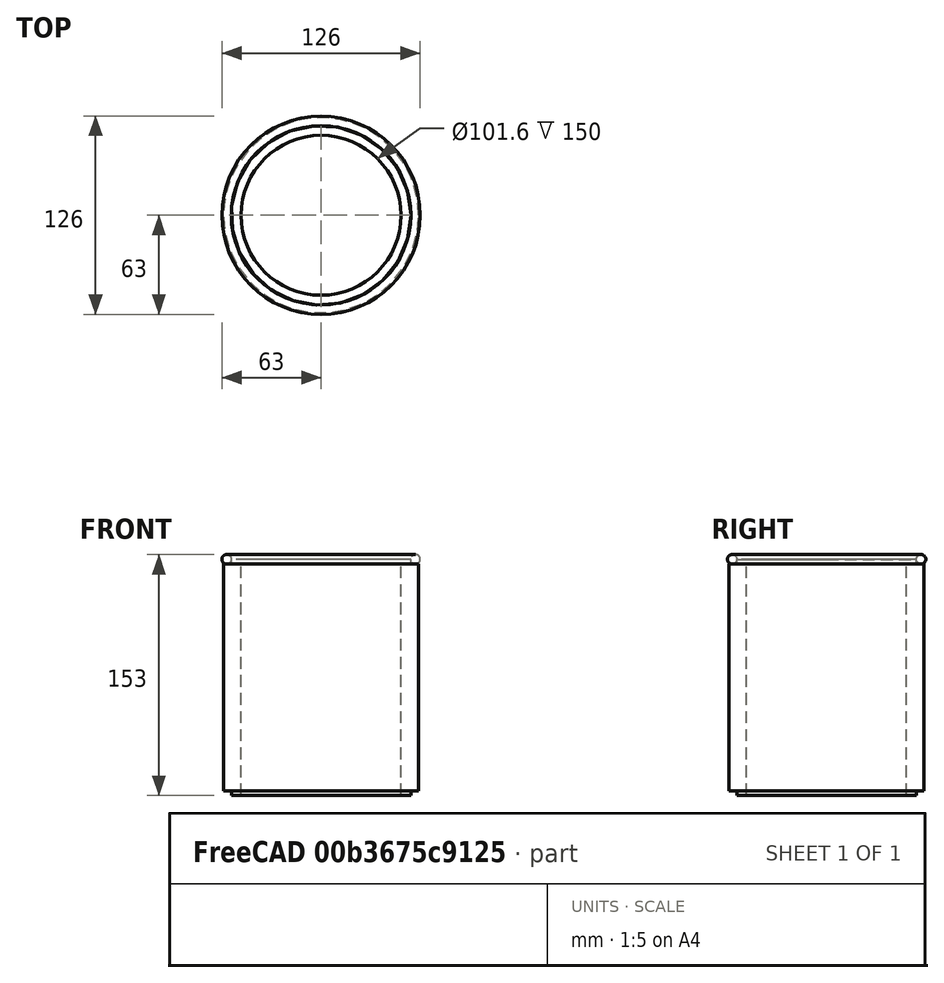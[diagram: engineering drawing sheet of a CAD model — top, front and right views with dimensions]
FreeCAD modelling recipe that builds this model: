
FCSTD DOCUMENT  (FreeCAD 0.17R13519 (Git))
Label: tube cad design
License: All rights reserved
LicenseURL: http://en.wikipedia.org/wiki/All_rights_reserved
objects: Part::Cylinder×18, Part::Cut×15, TechDraw::DrawViewDimension×7, TechDraw::DrawViewPart×5, Part::Torus×1, TechDraw::DrawSVGTemplate×1, TechDraw::DrawPage×1
note: 34 computed .brp shape members not serialized (recipe doc carries the construction recipe); baked Part::Feature solids carry a one-line shape summary decoded from their .brp

FEATURE [Part::Cylinder] Cylinder
  Angle = 360
  AttacherType = Attacher::AttachEngine3D
  Height = 150
  Radius = 61.91
FEATURE [Part::Cylinder] Cylinder001
  Angle = 360
  AttacherType = Attacher::AttachEngine3D
  Height = 150
  Radius = 50.8
FEATURE [Part::Cut] Cut
  Base = -> Cylinder
  Tool = -> Cylinder001
FEATURE [Part::Cylinder] Cylinder002
  Angle = 360
  AttacherType = Attacher::AttachEngine3D
  Height = 3
  Radius = 61.91
FEATURE [Part::Cylinder] Cylinder003
  Angle = 360
  AttacherType = Attacher::AttachEngine3D
  Height = 3
  Radius = 57
FEATURE [Part::Cut] Cut001
  Base = -> Cylinder002
  Tool = -> Cylinder003
FEATURE [Part::Cylinder] Cylinder004
  Angle = 360
  AttacherType = Attacher::AttachEngine3D
  Height = 3
  Radius = 61.91
FEATURE [Part::Cylinder] Cylinder005
  Angle = 360
  AttacherType = Attacher::AttachEngine3D
  Height = 3
  Radius = 57
FEATURE [Part::Cut] Cut002
  Base = -> Cylinder004
  Placement = pos=(0,0,147) rot=(0,0,1;0rad)
  Tool = -> Cylinder005
FEATURE [Part::Cut] Cut003
  Base = -> Cut
  Tool = -> Cut002
FEATURE [Part::Cut] Cut004
  Base = -> Cut003
  Placement = pos=(100,-500,0) rot=(0.707107,0,0.707107;0rad)
  Tool = -> Cut001
FEATURE [Part::Torus] Torus
  Angle1 = -180
  Angle2 = 180
  Angle3 = 360
  AttacherType = Attacher::AttachEngine3D
  Placement = pos=(100,-500,150) rot=(0,0,1;0rad)
  Radius1 = 60
  Radius2 = 3
FEATURE [TechDraw::DrawSVGTemplate] Template001
  EditableTexts = Designed_by_Name=Jake Hosen; FC-Date=July 2018; FC-Title=Title; Subtitle=Case Tube
  Height = 210
  Orientation = 1
  Width = 297
FEATURE [TechDraw::DrawViewPart] View003
  CoarseView = false
  Direction = (0,0,1)
  Focus = 100
  HardHidden = false
  IsoCount = 0
  IsoHidden = false
  IsoVisible = false
  LockPosition = false
  Perspective = false
  Rotation = 0
  Scale = 0.5
  ScaleType = 0
  SeamHidden = false
  SeamVisible = false
  SmoothHidden = false
  SmoothVisible = false
  Source = -> [Cut004]
  X = 78.5627
  Y = 140.236
FEATURE [TechDraw::DrawViewPart] View004
  CoarseView = false
  Direction = (-1,1,0)
  Focus = 100
  HardHidden = false
  IsoCount = 0
  IsoHidden = false
  IsoVisible = false
  LockPosition = false
  Perspective = false
  Rotation = 90
  Scale = 0.5
  ScaleType = 0
  SeamHidden = false
  SeamVisible = false
  SmoothHidden = false
  SmoothVisible = false
  Source = -> [Cut004]
  X = 189.733
  Y = 140.236
FEATURE [TechDraw::DrawViewDimension] Dimension
  FormatSpec = %.2f
  LockPosition = false
  MeasureType = 1
  References2D = -> [View004]
  Rotation = 0
  ScaleType = 0
  Type = 1
  X = 0
  Y = 0
FEATURE [TechDraw::DrawViewDimension] Dimension001
  FormatSpec = %.2f
  LockPosition = false
  MeasureType = 1
  Rotation = 0
  ScaleType = 0
  Type = 6
  X = -38.9727
  Y = -45.913
FEATURE [TechDraw::DrawViewDimension] Dimension002
  FormatSpec = %.2f
  LockPosition = false
  MeasureType = 1
  References2D = -> [View003]
  Rotation = 0
  ScaleType = 0
  Type = 5
  X = 14.1476
  Y = -10.9444
FEATURE [TechDraw::DrawViewPart] View
  CoarseView = false
  Direction = (-1,0,1)
  Focus = 100
  HardHidden = false
  IsoCount = 0
  IsoHidden = false
  IsoVisible = false
  LockPosition = false
  Perspective = false
  Rotation = 75
  Scale = 0.5
  ScaleType = 0
  SeamHidden = false
  SeamVisible = false
  SmoothHidden = false
  SmoothVisible = false
  Source = -> [Cut004]
  X = 77.228
  Y = 52.1466
FEATURE [TechDraw::DrawViewDimension] Dimension003
  FormatSpec = %.2f
  LockPosition = false
  MeasureType = 1
  References2D = -> [View004]
  Rotation = 0
  ScaleType = 0
  Type = 1
  X = 1.06774
  Y = -16.2831
FEATURE [TechDraw::DrawViewDimension] Dimension004
  FormatSpec = %.2f
  LockPosition = false
  MeasureType = 1
  References2D = -> [View003]
  Rotation = 0
  ScaleType = 0
  Type = 5
  X = 9.87664
  Y = 14.4146
FEATURE [TechDraw::DrawPage] Page002
  KeepUpdated = true
  ProjectionType = 0
  Template = -> Template001
  Views = -> [View003,View004,Dimension,Dimension001,Dimension002,View,Dimension003,Dimension004]
FEATURE [Part::Cylinder] Cylinder006
  Angle = 360
  AttacherType = Attacher::AttachEngine3D
  Height = 150
  Radius = 50.8
FEATURE [Part::Cylinder] Cylinder007
  Angle = 360
  AttacherType = Attacher::AttachEngine3D
  Height = 150
  Radius = 61.91
FEATURE [Part::Cylinder] Cylinder008
  Angle = 360
  AttacherType = Attacher::AttachEngine3D
  Height = 3
  Radius = 61.91
FEATURE [Part::Cylinder] Cylinder009
  Angle = 360
  AttacherType = Attacher::AttachEngine3D
  Height = 3
  Radius = 57
FEATURE [Part::Cut] Cut006
  Base = -> Cylinder008
  Placement = pos=(0,0,147) rot=(0,0,1;0rad)
  Tool = -> Cylinder009
FEATURE [Part::Cylinder] Cylinder010
  Angle = 360
  AttacherType = Attacher::AttachEngine3D
  Height = 3
  Radius = 57
FEATURE [Part::Cylinder] Cylinder011
  Angle = 360
  AttacherType = Attacher::AttachEngine3D
  Height = 3
  Radius = 61.91
FEATURE [Part::Cut] Cut007
  Base = -> Cylinder011
  Tool = -> Cylinder010
FEATURE [Part::Cut] Cut009
  Base = -> Cylinder007
  Tool = -> Cylinder006
FEATURE [Part::Cut] Cut008
  Base = -> Cut009
  Tool = -> Cut006
FEATURE [Part::Cut] Cut005
  Base = -> Cut008
  Placement = pos=(100,-500,0) rot=(0.707107,0,0.707107;0rad)
  Tool = -> Cut007
FEATURE [TechDraw::DrawViewPart] View005
  CoarseView = false
  Direction = (-1,1,0)
  Focus = 100
  HardHidden = false
  IsoCount = 0
  IsoHidden = false
  IsoVisible = false
  LockPosition = false
  Perspective = false
  Rotation = 90
  Scale = 0.5
  ScaleType = 0
  SeamHidden = false
  SeamVisible = false
  SmoothHidden = false
  SmoothVisible = false
  Source = -> [Cut005]
  X = 189.733
  Y = 140.236
FEATURE [TechDraw::DrawViewDimension] Dimension005
  FormatSpec = %.2f
  LockPosition = false
  MeasureType = 1
  References2D = -> [View005]
  Rotation = 0
  ScaleType = 0
  Type = 1
  X = 0
  Y = 0
FEATURE [Part::Cylinder] Cylinder012
  Angle = 360
  AttacherType = Attacher::AttachEngine3D
  Height = 150
  Radius = 50.8
FEATURE [Part::Cylinder] Cylinder013
  Angle = 360
  AttacherType = Attacher::AttachEngine3D
  Height = 150
  Radius = 61.91
FEATURE [Part::Cylinder] Cylinder014
  Angle = 360
  AttacherType = Attacher::AttachEngine3D
  Height = 3
  Radius = 61.91
FEATURE [Part::Cylinder] Cylinder015
  Angle = 360
  AttacherType = Attacher::AttachEngine3D
  Height = 3
  Radius = 57
FEATURE [Part::Cut] Cut011
  Base = -> Cylinder014
  Placement = pos=(0,0,147) rot=(0,0,1;0rad)
  Tool = -> Cylinder015
FEATURE [Part::Cylinder] Cylinder016
  Angle = 360
  AttacherType = Attacher::AttachEngine3D
  Height = 3
  Radius = 57
FEATURE [Part::Cylinder] Cylinder017
  Angle = 360
  AttacherType = Attacher::AttachEngine3D
  Height = 3
  Radius = 61.91
FEATURE [Part::Cut] Cut012
  Base = -> Cylinder017
  Tool = -> Cylinder016
FEATURE [Part::Cut] Cut014
  Base = -> Cylinder013
  Tool = -> Cylinder012
FEATURE [Part::Cut] Cut013
  Base = -> Cut014
  Tool = -> Cut011
FEATURE [Part::Cut] Cut010
  Base = -> Cut013
  Placement = pos=(100,-500,0) rot=(0.707107,0,0.707107;0rad)
  Tool = -> Cut012
FEATURE [TechDraw::DrawViewPart] View006
  CoarseView = false
  Direction = (-1,1,0)
  Focus = 100
  HardHidden = false
  IsoCount = 0
  IsoHidden = false
  IsoVisible = false
  LockPosition = false
  Perspective = false
  Rotation = 90
  Scale = 0.5
  ScaleType = 0
  SeamHidden = false
  SeamVisible = false
  SmoothHidden = false
  SmoothVisible = false
  Source = -> [Cut010]
  X = 189.733
  Y = 140.236
FEATURE [TechDraw::DrawViewDimension] Dimension006
  FormatSpec = %.2f
  LockPosition = false
  MeasureType = 1
  References2D = -> [View006]
  Rotation = 0
  ScaleType = 0
  Type = 1
  X = 1.06774
  Y = -16.2831
